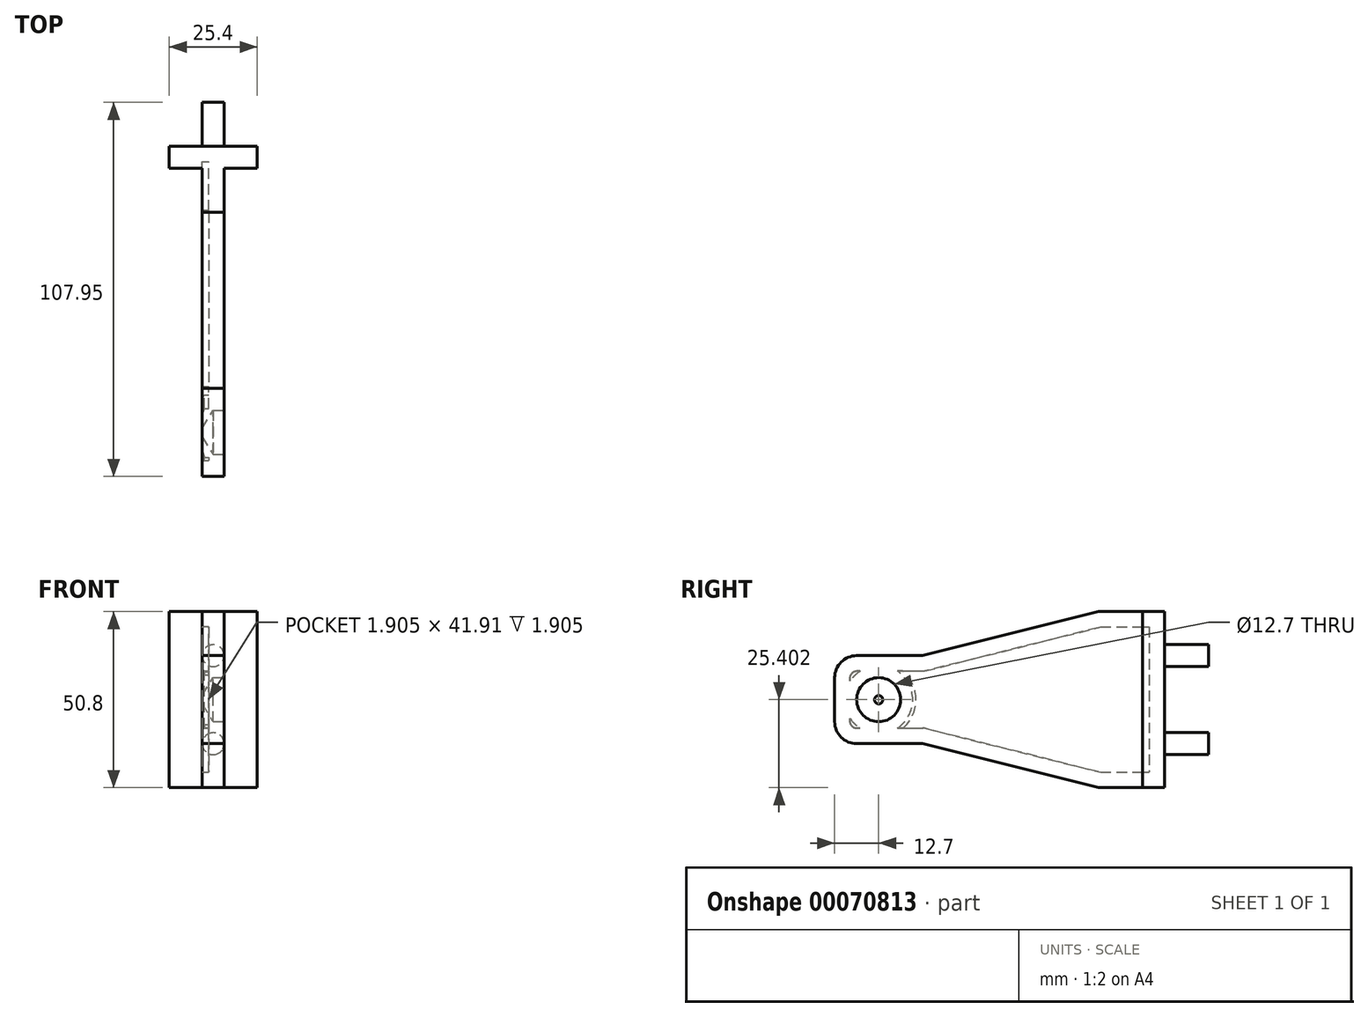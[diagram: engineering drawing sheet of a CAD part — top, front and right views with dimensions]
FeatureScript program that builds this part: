
annotation { "Feature Type Name" : "Feature", "Feature Type Description" : "" }
export const myFeature = defineFeature(function(context is Context, id is Id, definition is map)
    precondition{}
    {
        {
            var Q0;
            Q0=qCreatedBy(makeId("Front.planeOp"),FACE);
            var sketch = newSketch(context, id + "F0", { "sketchPlane" : qUnion([Q0])});
            skLineSegment(sketch, "E0", {"start": v(-19.3, 37.74) * mm, "end": v(6.1, 37.74) * mm});
            skLineSegment(sketch, "E1", {"start": v(6.1, 37.74) * mm, "end": v(6.1, -13.06) * mm});
            skLineSegment(sketch, "E2", {"start": v(6.1, -13.06) * mm, "end": v(-19.3, -13.06) * mm});
            skLineSegment(sketch, "E3", {"start": v(-19.3, -13.06) * mm, "end": v(-19.3, 37.74) * mm});
            skSolve(sketch);
        }
        {
            var Q0;
            Q0 = qSketchRegion(id + "F0", true);
            extrude(context, id + "F1", {"entities" : qUnion([Q0]), "depth" : 6.35 * mm});
        }
        {
            var Q0;
            Q0=makeQuery(id+"F1.opExtrude","CAP_FACE",FACE,{"disambiguationData":[OSD([sQuery(id+"F0.wireOp",EDGE,"E0"),sQuery(id+"F0.wireOp",EDGE,"E1"),sQuery(id+"F0.wireOp",EDGE,"E2"),sQuery(id+"F0.wireOp",EDGE,"E3")])],"isStart":false});
            var sketch = newSketch(context, id + "F2", { "sketchPlane" : qUnion([Q0])});
            skLineSegment(sketch, "E4", {"start": v(-9.77, 37.74) * mm, "end": v(-3.42, 37.74) * mm});
            skLineSegment(sketch, "E5", {"start": v(-3.42, 37.74) * mm, "end": v(-3.42, -13.06) * mm});
            skLineSegment(sketch, "E6", {"start": v(-3.42, -13.06) * mm, "end": v(-9.77, -13.06) * mm});
            skLineSegment(sketch, "E7", {"start": v(-9.77, -13.06) * mm, "end": v(-9.77, 37.74) * mm});
            skSolve(sketch);
        }
        {
            var Q0;
            Q0 = qSketchRegion(id + "F2", true);
            extrude(context, id + "F3", {"entities" : qUnion([Q0]), "operationType" : NewBodyOperationType.ADD, "depth" : 12.7 * mm});
        }
        {
            var Q0;
            Q0=makeQuery(id+"F3.opExtrude","CAP_FACE",FACE,{"disambiguationData":[OSD([sQuery(id+"F2.wireOp",EDGE,"E4"),sQuery(id+"F2.wireOp",EDGE,"E5"),sQuery(id+"F2.wireOp",EDGE,"E6"),sQuery(id+"F2.wireOp",EDGE,"E7")])],"isStart":false});
            cPlane(context, id + "F4", {"entities" : qUnion([Q0]), "cplaneType" : CPlaneType.OFFSET, "offset" : 50.8 * mm, "width" : 152.4 * mm, "height" : 152.4 * mm});
        }
        {
            var Q0;
            Q0=qCreatedBy(id+"F4.planeOp",FACE);
            var sketch = newSketch(context, id + "F5", { "sketchPlane" : qUnion([Q0])});
            skLineSegment(sketch, "E8", {"start": v(-9.85, 25.04) * mm, "end": v(-9.85, -0.36) * mm});
            skLineSegment(sketch, "E9", {"start": v(-9.85, -0.36) * mm, "end": v(-3.5, -0.36) * mm});
            skLineSegment(sketch, "E10", {"start": v(-3.5, -0.36) * mm, "end": v(-3.5, 25.04) * mm});
            skLineSegment(sketch, "E11", {"start": v(-3.5, 25.04) * mm, "end": v(-9.85, 25.04) * mm});
            skLineSegment(sketch, "E12.0", {"start": v(-9.77, -0.36) * mm, "end": v(-9.77, 25.04) * mm});
            skSolve(sketch);
        }
        {
            var Q1;
            Q1=makeQuery(id+"F3.opExtrude","CAP_FACE",FACE,{"disambiguationData":[OSD([sQuery(id+"F2.wireOp",EDGE,"E4"),sQuery(id+"F2.wireOp",EDGE,"E5"),sQuery(id+"F2.wireOp",EDGE,"E6"),sQuery(id+"F2.wireOp",EDGE,"E7")])],"isStart":false});
            var Q2;
            {var subQ0=sQuery(id+"F5.wireOp",EDGE,"E10");Q2=makeQuery(id+"F5.imprint","IMPRINT",FACE,{"disambiguationData":[TD([[makeQuery(id+"F5.imprint","IMPRINT",EDGE,{"derivedFrom":subQ0}),1.0]])]});}
            loft(context, id + "F6", {"operationType" : NewBodyOperationType.ADD, "sheetProfilesArray" : [{ "sheetProfileEntities" : qUnion([Q1]) }, { "sheetProfileEntities" : qUnion([Q2]) }]});
        }
        {
            var Q0;
            {var subQ0=sQuery(id+"F5.wireOp",EDGE,"E10");Q0=makeQuery(id+"F6.opLoft","CAP_FACE",FACE,{"disambiguationData":[OSD([makeQuery(id+"F5.imprint","IMPRINT",FACE,{"disambiguationData":[TD([[makeQuery(id+"F5.imprint","IMPRINT",EDGE,{"derivedFrom":subQ0}),1.0]])]})])],"isStart":true});}
            extrude(context, id + "F7", {"entities" : qUnion([Q0]), "operationType" : NewBodyOperationType.ADD, "depth" : 25.4 * mm});
        }
        {
            var Q0;
            Q0=makeQuery(id+"F7.opExtrude","CAP_EDGE",EDGE,{"disambiguationData":[OSD([sQuery(id+"F5.wireOp",EDGE,"E10"),sQuery(id+"F5.wireOp",EDGE,"E11"),sQuery(id+"F5.wireOp",EDGE,"E12.0")])],"isStart":false});
            var Q1;
            Q1=makeQuery(id+"F7.opExtrude","CAP_EDGE",EDGE,{"disambiguationData":[OSD([sQuery(id+"F5.wireOp",EDGE,"E9"),sQuery(id+"F5.wireOp",EDGE,"E10"),sQuery(id+"F5.wireOp",EDGE,"E12.0")])],"isStart":false});
            fillet(context, id + "F8", {"entities" : qUnion([Q0, Q1]), "radius" : 6.35 * mm, "tangentPropagation" : true, "allowEdgeOverflow" : false});
        }
        {
            var Q0;
            Q0=makeQuery(id+"F7.opExtrude","SWEPT_FACE",FACE,{"disambiguationData":[OSD([sQuery(id+"F5.wireOp",EDGE,"E9"),sQuery(id+"F5.wireOp",EDGE,"E10"),sQuery(id+"F5.wireOp",EDGE,"E11")])]});
            var sketch = newSketch(context, id + "F9", { "sketchPlane" : qUnion([Q0])});
            skPoint(sketch, "E13", {"position": v(-82.55, 12.34) * mm});
            skPoint(sketch, "E13.positionSnap0", {"position": v(-95.25, 12.34) * mm});
            skSolve(sketch);
        }
        {
            var Q0;
            Q0=sQuery(id+"F9.wireOp",VERTEX,"E13");
            var Q1;
            Q1=makeQuery(id+"F1.opExtrude","SWEPT_BODY",BODY,{"disambiguationData":[OSD([sQuery(id+"F0.wireOp",EDGE,"E0"),sQuery(id+"F0.wireOp",EDGE,"E1"),sQuery(id+"F0.wireOp",EDGE,"E2"),sQuery(id+"F0.wireOp",EDGE,"E3")])]});
            hole(context, id + "F10", {"style" : HoleStyle.SIMPLE, "holeDiameter" : 12.7 * mm, "endStyle" : HoleEndStyle.BLIND, "holeDepth" : 3.17 * mm, "locations" : qUnion([Q0]), "scope" : qUnion([Q1])});
        }
        {
            var Q0;
            {var subQ0=sQuery(id+"F5.wireOp",EDGE,"E12.0");var subQ1=sQuery(id+"F5.wireOp",EDGE,"E11");var subQ2=sQuery(id+"F5.wireOp",EDGE,"E9");var subQ3=sQuery(id+"F2.wireOp",EDGE,"E7");Q0=makeQuery(id+"F7.boolean.opBoolean","MERGE",FACE,{"derivedFrom":[makeQuery(id+"F6.boolean.opBoolean","MERGE",FACE,{"derivedFrom":[makeQuery(id+"F3.opExtrude","SWEPT_FACE",FACE,{"disambiguationData":[OSD([subQ3])]}),makeQuery(id+"F6.opLoft","SWEPT_FACE",FACE,{"disambiguationData":[OSD([sQuery(id+"F0.wireOp",EDGE,"E0"),sQuery(id+"F0.wireOp",EDGE,"E2"),sQuery(id+"F2.wireOp",EDGE,"E4"),sQuery(id+"F2.wireOp",EDGE,"E6"),subQ3,subQ2,subQ1,subQ0])]})]}),makeQuery(id+"F7.opExtrude","SWEPT_FACE",FACE,{"disambiguationData":[OSD([subQ2,subQ1,subQ0])]})]});}
            shell(context, id + "F11", {"entities" : qUnion([Q0]), "thickness" : 4.44 * mm});
        }
        {
            var Q0;
            Q0=makeQuery(id+"F1.opExtrude","CAP_FACE",FACE,{"disambiguationData":[OSD([sQuery(id+"F0.wireOp",EDGE,"E0"),sQuery(id+"F0.wireOp",EDGE,"E1"),sQuery(id+"F0.wireOp",EDGE,"E2"),sQuery(id+"F0.wireOp",EDGE,"E3")])],"isStart":true});
            var sketch = newSketch(context, id + "F12", { "sketchPlane" : qUnion([Q0])});
            skCircle(sketch, "E14", {"center": v(6.6, 25.04) * mm, "radius": 3.18 * mm});
            skPoint(sketch, "E14.centerSnap0", {"position": v(6.6, 37.74) * mm});
            skCircle(sketch, "E15", {"center": v(6.6, -0.36) * mm, "radius": 3.18 * mm});
            skPoint(sketch, "E15.centerSnap0", {"position": v(6.6, -13.06) * mm});
            skSolve(sketch);
        }
        {
            var Q0;
            Q0=makeQuery(id+"F12.imprint","IMPRINT",FACE,{"disambiguationData":[TD([[makeQuery(id+"F12.imprint","IMPRINT",EDGE,{"derivedFrom":sQuery(id+"F12.wireOp",EDGE,"E14")}),1.0]])]});
            var Q1;
            Q1=makeQuery(id+"F12.imprint","IMPRINT",FACE,{"disambiguationData":[TD([[makeQuery(id+"F12.imprint","IMPRINT",EDGE,{"derivedFrom":sQuery(id+"F12.wireOp",EDGE,"E15")}),1.0]])]});
            var Q2;
            Q2=sQuery(id+"F12.wireOp",EDGE,"E14");
            var Q3;
            Q3=sQuery(id+"F12.wireOp",EDGE,"E15");
            extrude(context, id + "F13", {"entities" : qUnion([Q0, Q1]), "operationType" : NewBodyOperationType.ADD, "surfaceEntities" : qUnion([Q2, Q3]), "depth" : 12.7 * mm});
        }
    });
